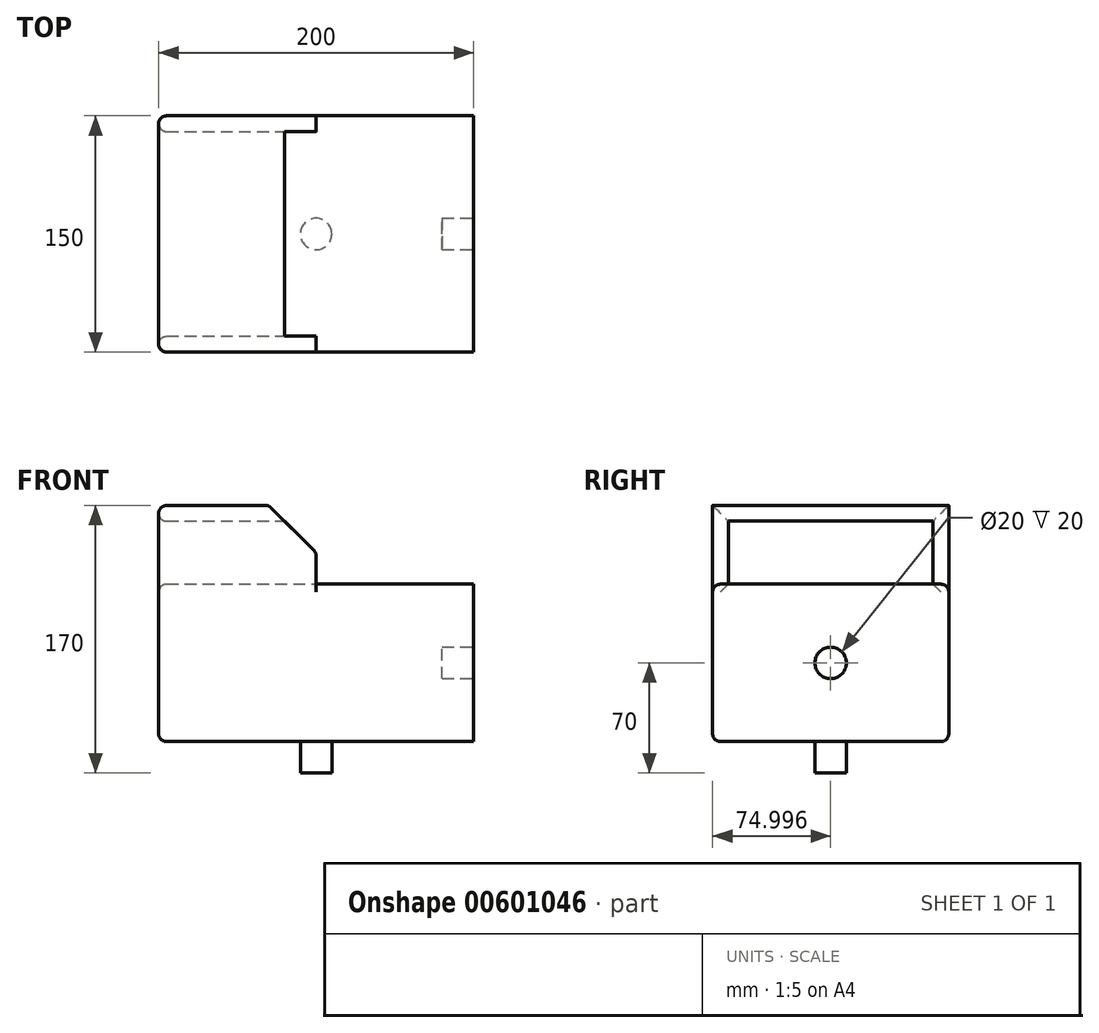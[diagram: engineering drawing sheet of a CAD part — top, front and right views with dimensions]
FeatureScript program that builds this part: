
annotation { "Feature Type Name" : "Feature", "Feature Type Description" : "" }
export const myFeature = defineFeature(function(context is Context, id is Id, definition is map)
    precondition{}
    {
        {
            var Q0;
            Q0=qCreatedBy(makeId("Top.planeOp"),FACE);
            var sketch = newSketch(context, id + "F0", { "sketchPlane" : qUnion([Q0])});
            skLineSegment(sketch, "E0.bottom", {"start": v(-114.71, 82.17) * mm, "end": v(85.29, 82.17) * mm});
            skLineSegment(sketch, "E0.top", {"start": v(-114.71, -67.83) * mm, "end": v(85.29, -67.83) * mm});
            skLineSegment(sketch, "E0.left", {"start": v(-114.71, 82.17) * mm, "end": v(-114.71, -67.83) * mm});
            skLineSegment(sketch, "E0.right", {"start": v(85.29, 82.17) * mm, "end": v(85.29, -67.83) * mm});
            skCircle(sketch, "E1", {"center": v(-14.71, 7.17) * mm, "radius": 10 * mm});
            skPoint(sketch, "E1.centerSnap0", {"position": v(85.29, 7.17) * mm});
            skPoint(sketch, "E1.centerSnap1", {"position": v(-14.71, 82.17) * mm});
            skSolve(sketch);
        }
        {
            var Q0;
            Q0 = qSketchRegion(id + "F0", true);
            var Q1;
            Q1=makeQuery(id+"F0.imprint","IMPRINT",FACE,{"disambiguationData":[TD([[makeQuery(id+"F0.imprint","IMPRINT",EDGE,{"derivedFrom":sQuery(id+"F0.wireOp",EDGE,"E1")}),1.0]])]});
            extrude(context, id + "F1", {"entities" : qUnion([Q0, Q1]), "depth" : 100 * mm, "offsetDistance" : 25 * mm});
        }
        {
            var Q0;
            Q0=makeQuery(id+"F0.imprint","IMPRINT",FACE,{"disambiguationData":[TD([[makeQuery(id+"F0.imprint","IMPRINT",EDGE,{"derivedFrom":sQuery(id+"F0.wireOp",EDGE,"E1")}),1.0]])]});
            extrude(context, id + "F2", {"entities" : qUnion([Q0]), "operationType" : NewBodyOperationType.ADD, "oppositeDirection" : true, "depth" : 20 * mm, "offsetDistance" : 25 * mm});
        }
        {
            var Q0;
            Q0=makeQuery(id+"F1.opExtrude","CAP_FACE",FACE,{"disambiguationData":[OSD([sQuery(id+"F0.wireOp",EDGE,"E0.bottom"),sQuery(id+"F0.wireOp",EDGE,"E0.top"),sQuery(id+"F0.wireOp",EDGE,"E0.left"),sQuery(id+"F0.wireOp",EDGE,"E0.right")])],"isStart":false});
            var sketch = newSketch(context, id + "F3", { "sketchPlane" : qUnion([Q0])});
            skPoint(sketch, "E2.oppositeSnap0", {"position": v(-14.71, 82.17) * mm});
            skLineSegment(sketch, "E2.bottom", {"start": v(-114.71, 82.17) * mm, "end": v(-14.71, 82.17) * mm});
            skLineSegment(sketch, "E2.top", {"start": v(-114.71, 72.17) * mm, "end": v(-14.71, 72.17) * mm});
            skLineSegment(sketch, "E2.left", {"start": v(-114.71, 82.17) * mm, "end": v(-114.71, 72.17) * mm});
            skLineSegment(sketch, "E2.right", {"start": v(-14.71, 82.17) * mm, "end": v(-14.71, 72.17) * mm});
            skPoint(sketch, "E3.oppositeSnap0", {"position": v(-14.71, -67.83) * mm});
            skLineSegment(sketch, "E3.bottom", {"start": v(-114.71, -67.83) * mm, "end": v(-14.71, -67.83) * mm});
            skLineSegment(sketch, "E3.top", {"start": v(-114.71, -57.83) * mm, "end": v(-14.71, -57.83) * mm});
            skLineSegment(sketch, "E3.left", {"start": v(-114.71, -67.83) * mm, "end": v(-114.71, -57.83) * mm});
            skLineSegment(sketch, "E3.right", {"start": v(-14.71, -67.83) * mm, "end": v(-14.71, -57.83) * mm});
            skSolve(sketch);
        }
        {
            var Q0;
            Q0 = qSketchRegion(id + "F3", true);
            extrude(context, id + "F4", {"entities" : qUnion([Q0]), "operationType" : NewBodyOperationType.ADD, "depth" : 50 * mm, "offsetDistance" : 25 * mm});
        }
        {
            var Q0;
            Q0=makeQuery(id+"F4.opExtrude","CAP_EDGE",EDGE,{"disambiguationData":[OSD([sQuery(id+"F3.wireOp",EDGE,"E3.right")])],"isStart":false});
            var Q1;
            Q1=makeQuery(id+"F4.opExtrude","CAP_EDGE",EDGE,{"disambiguationData":[OSD([sQuery(id+"F3.wireOp",EDGE,"E2.right")])],"isStart":false});
            chamfer(context, id + "F5", {"entities" : qUnion([Q0, Q1]), "width" : 30 * mm, "tangentPropagation" : true});
        }
        {
            var Q0;
            Q0=makeQuery(id+"F4.opExtrude","SWEPT_FACE",FACE,{"disambiguationData":[OSD([sQuery(id+"F3.wireOp",EDGE,"E2.top")])]});
            var sketch = newSketch(context, id + "F6", { "sketchPlane" : qUnion([Q0])});
            skLineSegment(sketch, "E4.bottom", {"start": v(-114.71, 150) * mm, "end": v(-44.71, 150) * mm});
            skLineSegment(sketch, "E4.top", {"start": v(-114.71, 140) * mm, "end": v(-44.71, 140) * mm});
            skLineSegment(sketch, "E4.left", {"start": v(-114.71, 150) * mm, "end": v(-114.71, 140) * mm});
            skLineSegment(sketch, "E4.right", {"start": v(-44.71, 150) * mm, "end": v(-44.71, 140) * mm});
            skLineSegment(sketch, "E5", {"start": v(-44.71, 140) * mm, "end": v(-34.71, 140) * mm});
            skLineSegment(sketch, "E6", {"start": v(-44.71, 150) * mm, "end": v(-34.71, 140) * mm});
            skSolve(sketch);
        }
        {
            var Q0;
            Q0 = qSketchRegion(id + "F6", true);
            extrude(context, id + "F7", {"entities" : qUnion([Q0]), "operationType" : NewBodyOperationType.ADD, "depth" : 130 * mm, "offsetDistance" : 25 * mm});
        }
        {
            var Q0;
            Q0=makeQuery(id+"F1.opExtrude","CAP_EDGE",EDGE,{"disambiguationData":[OSD([sQuery(id+"F0.wireOp",EDGE,"E0.bottom")])],"isStart":false});
            var Q1;
            Q1=makeQuery(id+"F1.opExtrude","CAP_EDGE",EDGE,{"disambiguationData":[OSD([sQuery(id+"F0.wireOp",EDGE,"E0.top")])],"isStart":false});
            var Q2;
            Q2=makeQuery(id+"F1.opExtrude","CAP_EDGE",EDGE,{"disambiguationData":[OSD([sQuery(id+"F0.wireOp",EDGE,"E0.bottom")])],"isStart":true});
            var Q3;
            Q3=makeQuery(id+"F1.opExtrude","CAP_EDGE",EDGE,{"disambiguationData":[OSD([sQuery(id+"F0.wireOp",EDGE,"E0.top")])],"isStart":true});
            var Q4;
            Q4=makeQuery(id+"F7.boolean.opBoolean","MERGE",FACE,{"derivedFrom":[makeQuery(id+"F4.boolean.opBoolean","MERGE",FACE,{"derivedFrom":[makeQuery(id+"F1.opExtrude","SWEPT_FACE",FACE,{"disambiguationData":[OSD([sQuery(id+"F0.wireOp",EDGE,"E0.left")])]}),makeQuery(id+"F4.opExtrude","SWEPT_FACE",FACE,{"disambiguationData":[OSD([sQuery(id+"F3.wireOp",EDGE,"E2.left")])]}),makeQuery(id+"F4.opExtrude","SWEPT_FACE",FACE,{"disambiguationData":[OSD([sQuery(id+"F3.wireOp",EDGE,"E3.left")])]})]}),makeQuery(id+"F7.opExtrude","SWEPT_FACE",FACE,{"disambiguationData":[OSD([sQuery(id+"F6.wireOp",EDGE,"E4.left")])]})]});
            var Q5;
            {var subQ0=sQuery(id+"F3.wireOp",EDGE,"E3.right");Q5=makeQuery(id+"F5.opChamfer","BLEND_EDGE",EDGE,{"blendedFrom":[makeQuery(id+"F4.opExtrude","CAP_EDGE",EDGE,{"disambiguationData":[OSD([subQ0])],"isStart":false}),makeQuery(id+"F4.opExtrude","SWEPT_FACE",FACE,{"disambiguationData":[OSD([subQ0])]})],"blendedInto":[makeQuery(id+"F4.opExtrude","SWEPT_FACE",FACE,{"disambiguationData":[OSD([subQ0])]})]});}
            var Q6;
            {var subQ0=sQuery(id+"F3.wireOp",EDGE,"E3.right");var subQ1=sQuery(id+"F3.wireOp",EDGE,"E2.right");Q6=makeQuery(id+"F7.boolean.opBoolean","MERGE",EDGE,{"derivedFrom":[makeQuery(id+"F5.opChamfer","BLEND_EDGE",EDGE,{"blendedFrom":[makeQuery(id+"F4.opExtrude","CAP_EDGE",EDGE,{"disambiguationData":[OSD([subQ1])],"isStart":false}),makeQuery(id+"F4.opExtrude","CAP_FACE",FACE,{"disambiguationData":[OSD([sQuery(id+"F3.wireOp",EDGE,"E2.bottom"),sQuery(id+"F3.wireOp",EDGE,"E2.top"),sQuery(id+"F3.wireOp",EDGE,"E2.left"),subQ1])],"isStart":false})],"blendedInto":[makeQuery(id+"F4.opExtrude","CAP_FACE",FACE,{"disambiguationData":[OSD([sQuery(id+"F3.wireOp",EDGE,"E2.bottom"),sQuery(id+"F3.wireOp",EDGE,"E2.top"),sQuery(id+"F3.wireOp",EDGE,"E2.left"),subQ1])],"isStart":false})]}),makeQuery(id+"F5.opChamfer","BLEND_EDGE",EDGE,{"blendedFrom":[makeQuery(id+"F4.opExtrude","CAP_EDGE",EDGE,{"disambiguationData":[OSD([subQ0])],"isStart":false}),makeQuery(id+"F4.opExtrude","CAP_FACE",FACE,{"disambiguationData":[OSD([sQuery(id+"F3.wireOp",EDGE,"E3.bottom"),sQuery(id+"F3.wireOp",EDGE,"E3.top"),sQuery(id+"F3.wireOp",EDGE,"E3.left"),subQ0])],"isStart":false})],"blendedInto":[makeQuery(id+"F4.opExtrude","CAP_FACE",FACE,{"disambiguationData":[OSD([sQuery(id+"F3.wireOp",EDGE,"E3.bottom"),sQuery(id+"F3.wireOp",EDGE,"E3.top"),sQuery(id+"F3.wireOp",EDGE,"E3.left"),subQ0])],"isStart":false})]}),makeQuery(id+"F7.opExtrude","SWEPT_EDGE",EDGE,{"disambiguationData":[OSD([sQuery(id+"F6.wireOp",EDGE,"E4.bottom"),sQuery(id+"F6.wireOp",EDGE,"E4.right"),sQuery(id+"F6.wireOp",EDGE,"E6")])]})]});}
            var Q7;
            {var subQ0=sQuery(id+"F3.wireOp",EDGE,"E2.right");Q7=makeQuery(id+"F5.opChamfer","BLEND_EDGE",EDGE,{"blendedFrom":[makeQuery(id+"F4.opExtrude","CAP_EDGE",EDGE,{"disambiguationData":[OSD([subQ0])],"isStart":false}),makeQuery(id+"F4.opExtrude","SWEPT_FACE",FACE,{"disambiguationData":[OSD([subQ0])]})],"blendedInto":[makeQuery(id+"F4.opExtrude","SWEPT_FACE",FACE,{"disambiguationData":[OSD([subQ0])]})]});}
            fillet(context, id + "F8", {"entities" : qUnion([Q0, Q1, Q2, Q3, Q4, Q5, Q6, Q7]), "radius" : 5 * mm, "tangentPropagation" : true, "allowEdgeOverflow" : false});
        }
        {
            var Q0;
            Q0=makeQuery(id+"F1.opExtrude","SWEPT_FACE",FACE,{"disambiguationData":[OSD([sQuery(id+"F0.wireOp",EDGE,"E0.right")])]});
            var sketch = newSketch(context, id + "F9", { "sketchPlane" : qUnion([Q0])});
            skCircle(sketch, "E7", {"center": v(7.17, 50) * mm, "radius": 10 * mm});
            skPoint(sketch, "E7.centerSnap0", {"position": v(7.17, 100) * mm});
            skPoint(sketch, "E7.centerSnap1", {"position": v(-67.83, 50) * mm});
            skSolve(sketch);
        }
        {
            var Q0;
            Q0 = qSketchRegion(id + "F9", true);
            extrude(context, id + "F10", {"entities" : qUnion([Q0]), "operationType" : NewBodyOperationType.REMOVE, "oppositeDirection" : true, "depth" : 20 * mm, "offsetDistance" : 25 * mm});
        }
    });
